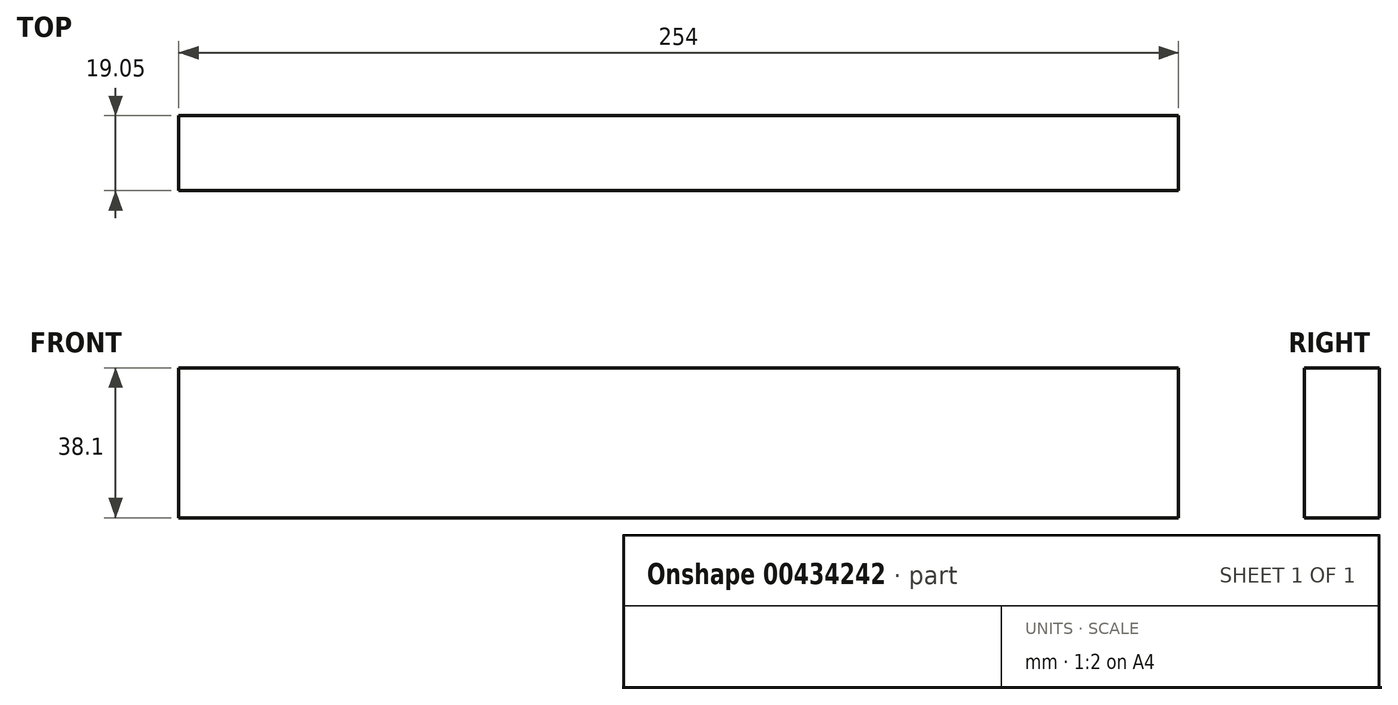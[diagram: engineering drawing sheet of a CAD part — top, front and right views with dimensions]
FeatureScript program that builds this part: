
annotation { "Feature Type Name" : "Feature", "Feature Type Description" : "" }
export const myFeature = defineFeature(function(context is Context, id is Id, definition is map)
    precondition{}
    {
        {
            var Q0;
            Q0=qCreatedBy(makeId("Front.planeOp"),FACE);
            var sketch = newSketch(context, id + "F0", { "sketchPlane" : qUnion([Q0])});
            skLineSegment(sketch, "E0.bottom", {"start": v(0, 0) * mm, "end": v(254, 0) * mm});
            skLineSegment(sketch, "E0.top", {"start": v(0, 38.1) * mm, "end": v(254, 38.1) * mm});
            skLineSegment(sketch, "E0.left", {"start": v(0, 0) * mm, "end": v(0, 38.1) * mm});
            skLineSegment(sketch, "E0.right", {"start": v(254, 0) * mm, "end": v(254, 38.1) * mm});
            skSolve(sketch);
        }
        {
            var Q0;
            Q0 = qSketchRegion(id + "F0", true);
            extrude(context, id + "F1", {"entities" : qUnion([Q0]), "depth" : 19.05 * mm});
        }
    });
